SOLIDWORKS PART (.sldprt)
format: sldprt  version: not decoded by parser v0  size: 128,512 bytes
history: native  units: mm
features: plane x3, sketch x3, cut_extrude x2, material x1, extrude x1 (+13 scaffold rows collapsed)
feature tree (23):
  scaffold x13  (default folders/planes/origin — collapsed)
  material  "Matériau <non spécifié>"
  plane  "Plan de face"
  plane  "Plan de dessus"
  plane  "Plan de droite"
  sketch  "Esquisse1"  dims[D1=38.0mm]
  extrude  "Extrusion1"  Depth=10mm
  sketch  "Esquisse3"  dims[D1=~12.454192mm]
  cut_extrude  "Extrusion3"  Depth=8mm
  sketch  "Esquisse4"  dims[D1=5.0mm]
  cut_extrude  "Extrusion4"  Depth=2mm
decode coverage: 6 of 6 modeling features carry decoded parameters
note: ~ marks probable driven/reference dimensions
note: suppression state not decoded; provenance and decode notes live in map.json
